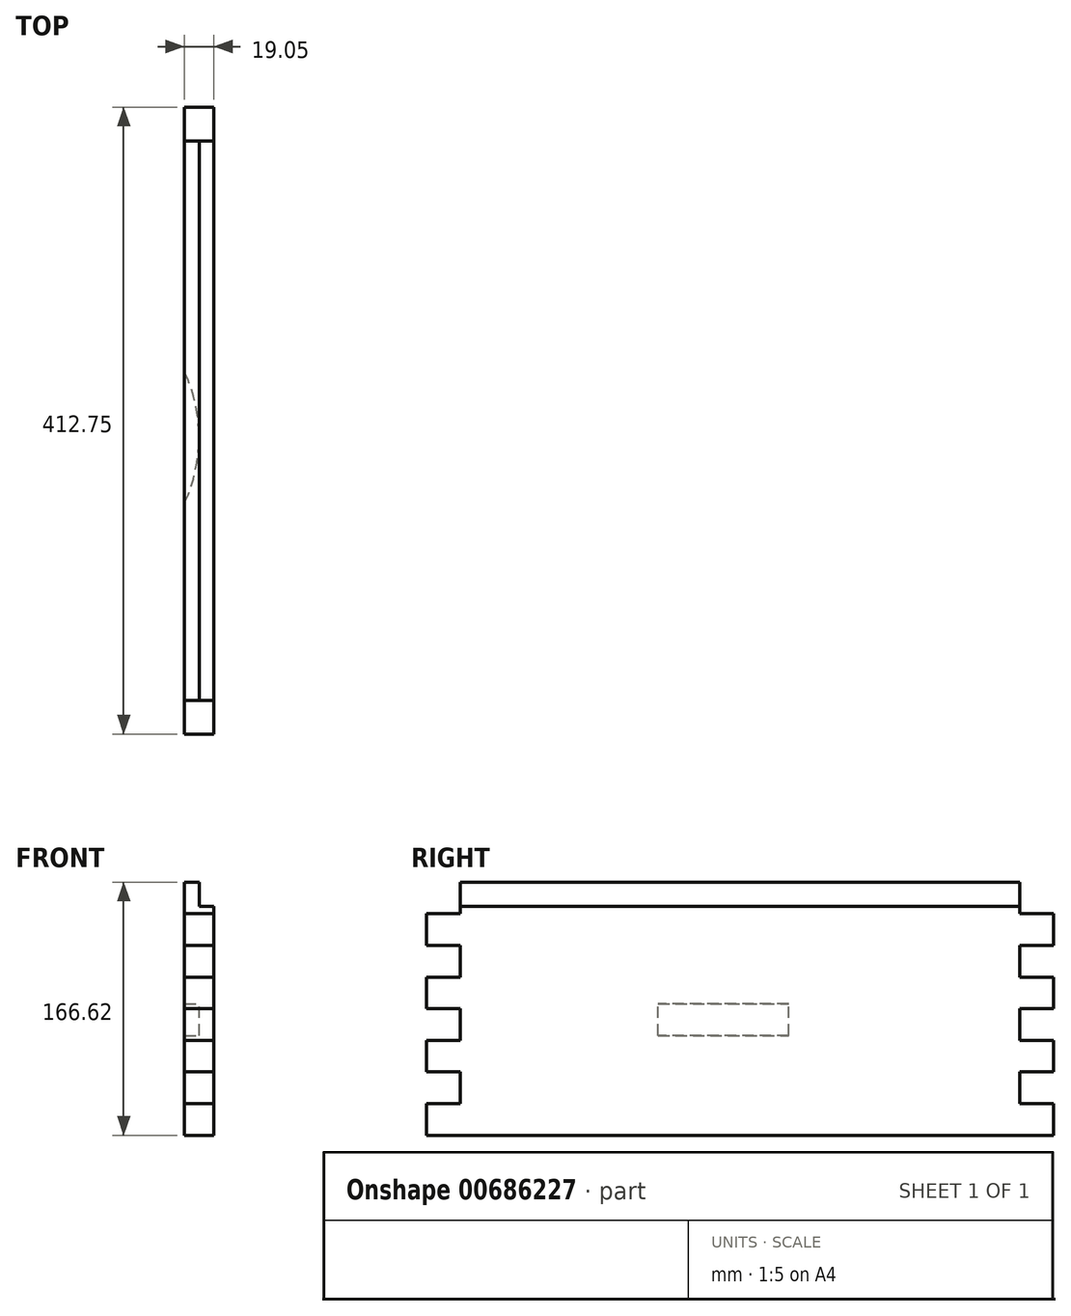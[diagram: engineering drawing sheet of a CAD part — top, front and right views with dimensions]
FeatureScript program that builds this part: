
annotation { "Feature Type Name" : "Feature", "Feature Type Description" : "" }
export const myFeature = defineFeature(function(context is Context, id is Id, definition is map)
    precondition{}
    {
        {
            var Q0;
            Q0=qCreatedBy(makeId("Front.planeOp"),FACE);
            var sketch = newSketch(context, id + "F0", { "sketchPlane" : qUnion([Q0])});
            skLineSegment(sketch, "E0.bottom", {"start": v(0, 0) * mm, "end": v(-19.05, 0) * mm});
            skLineSegment(sketch, "E0.top", {"start": v(0, 166.62) * mm, "end": v(-19.05, 166.62) * mm});
            skLineSegment(sketch, "E0.left", {"start": v(0, 0) * mm, "end": v(0, 166.62) * mm});
            skLineSegment(sketch, "E0.right", {"start": v(-19.05, 0) * mm, "end": v(-19.05, 166.62) * mm});
            skSolve(sketch);
        }
        {
            var Q0;
            Q0 = qSketchRegion(id + "F0", true);
            extrude(context, id + "F1", {"entities" : qUnion([Q0]), "oppositeDirection" : true, "depth" : 206.38 * mm, "offsetDistance" : 25.4 * mm});
        }
        {
            var Q0;
            Q0=qCreatedBy(makeId("Right.planeOp"),FACE);
            var sketch = newSketch(context, id + "F2", { "sketchPlane" : qUnion([Q0])});
            skLineSegment(sketch, "E1.bottom", {"start": v(0, 20.83) * mm, "end": v(22.23, 20.83) * mm});
            skLineSegment(sketch, "E1.top", {"start": v(0, 41.66) * mm, "end": v(22.23, 41.66) * mm});
            skLineSegment(sketch, "E1.left", {"start": v(0, 20.83) * mm, "end": v(0, 41.66) * mm});
            skLineSegment(sketch, "E1.right", {"start": v(22.23, 20.83) * mm, "end": v(22.23, 41.66) * mm});
            skLineSegment(sketch, "E2.bottom", {"start": v(0, 62.48) * mm, "end": v(22.23, 62.48) * mm});
            skLineSegment(sketch, "E2.top", {"start": v(0, 83.31) * mm, "end": v(22.23, 83.31) * mm});
            skLineSegment(sketch, "E2.left", {"start": v(0, 62.48) * mm, "end": v(0, 83.31) * mm});
            skLineSegment(sketch, "E2.right", {"start": v(22.23, 62.48) * mm, "end": v(22.23, 83.31) * mm});
            skLineSegment(sketch, "E3.bottom", {"start": v(0, 104.14) * mm, "end": v(22.23, 104.14) * mm});
            skLineSegment(sketch, "E3.top", {"start": v(0, 124.97) * mm, "end": v(22.23, 124.97) * mm});
            skLineSegment(sketch, "E3.left", {"start": v(0, 104.14) * mm, "end": v(0, 124.97) * mm});
            skLineSegment(sketch, "E3.right", {"start": v(22.23, 104.14) * mm, "end": v(22.22, 124.97) * mm});
            skLineSegment(sketch, "E4.bottom", {"start": v(0, 145.8) * mm, "end": v(22.22, 145.8) * mm});
            skLineSegment(sketch, "E4.top", {"start": v(0, 166.62) * mm, "end": v(22.22, 166.62) * mm});
            skLineSegment(sketch, "E4.left", {"start": v(0, 145.8) * mm, "end": v(0, 166.62) * mm});
            skLineSegment(sketch, "E4.right", {"start": v(22.22, 145.8) * mm, "end": v(22.22, 166.62) * mm});
            skLineSegment(sketch, "E5", {"start": v(22.22, 145.8) * mm, "end": v(22.23, 124.97) * mm, "construction": true});
            skLineSegment(sketch, "E6", {"start": v(22.23, 104.14) * mm, "end": v(22.23, 83.31) * mm, "construction": true});
            skLineSegment(sketch, "E7", {"start": v(22.23, 62.48) * mm, "end": v(22.23, 41.66) * mm, "construction": true});
            skLineSegment(sketch, "E8", {"start": v(22.23, 20.83) * mm, "end": v(22.23, 0) * mm, "construction": true});
            skSolve(sketch);
        }
        {
            var Q0;
            Q0 = qSketchRegion(id + "F2", true);
            extrude(context, id + "F3", {"entities" : qUnion([Q0]), "operationType" : NewBodyOperationType.REMOVE, "endBound" : BoundingType.THROUGH_ALL, "oppositeDirection" : true, "depth" : 25.4 * mm, "offsetDistance" : 25.4 * mm});
        }
        {
            var Q0;
            Q0=makeQuery(id+"F1.opExtrude","SWEPT_BODY",BODY,{"disambiguationData":[OSD([sQuery(id+"F0.wireOp",EDGE,"E0.bottom"),sQuery(id+"F0.wireOp",EDGE,"E0.top"),sQuery(id+"F0.wireOp",EDGE,"E0.left"),sQuery(id+"F0.wireOp",EDGE,"E0.right")])]});
            var Q1;
            Q1=makeQuery(id+"F1.opExtrude","CAP_FACE",FACE,{"disambiguationData":[OSD([sQuery(id+"F0.wireOp",EDGE,"E0.bottom"),sQuery(id+"F0.wireOp",EDGE,"E0.top"),sQuery(id+"F0.wireOp",EDGE,"E0.left"),sQuery(id+"F0.wireOp",EDGE,"E0.right")])],"isStart":false});
            mirror(context, id + "F4", {"operationType" : NewBodyOperationType.ADD, "entities" : qUnion([Q0]), "mirrorPlane" : qUnion([Q1])});
        }
        {
            var Q0;
            Q0=qCreatedBy(makeId("Front.planeOp"),FACE);
            var sketch = newSketch(context, id + "F5", { "sketchPlane" : qUnion([Q0])});
            skLineSegment(sketch, "E9.bottom", {"start": v(-9.53, 166.62) * mm, "end": v(0, 166.62) * mm});
            skLineSegment(sketch, "E9.top", {"start": v(-9.53, 150.75) * mm, "end": v(0, 150.75) * mm});
            skLineSegment(sketch, "E9.left", {"start": v(-9.53, 166.62) * mm, "end": v(-9.53, 150.75) * mm});
            skLineSegment(sketch, "E9.right", {"start": v(0, 166.62) * mm, "end": v(0, 150.75) * mm});
            skSolve(sketch);
        }
        {
            var Q0;
            Q0 = qSketchRegion(id + "F5", true);
            extrude(context, id + "F6", {"entities" : qUnion([Q0]), "operationType" : NewBodyOperationType.REMOVE, "endBound" : BoundingType.THROUGH_ALL, "oppositeDirection" : true, "depth" : 25.4 * mm, "offsetDistance" : 25.4 * mm});
        }
        {
            var Q0;
            Q0=qCreatedBy(makeId("Top.planeOp"),FACE);
            cPlane(context, id + "F7", {"entities" : qUnion([Q0]), "cplaneType" : CPlaneType.OFFSET, "offset" : 76.2 * mm, "width" : 152.4 * mm, "height" : 152.4 * mm});
        }
        {
            var Q0;
            Q0=qCreatedBy(id+"F7.planeOp",FACE);
            var sketch = newSketch(context, id + "F8", { "sketchPlane" : qUnion([Q0])});
            skCircle(sketch, "E10", {"center": v(-111.13, 195.26) * mm, "radius": 101.6 * mm});
            skLineSegment(sketch, "E11", {"start": v(-19.05, 390.53) * mm, "end": v(-19.05, 0) * mm, "construction": true});
            skLineSegment(sketch, "E12", {"start": v(-111.13, 195.26) * mm, "end": v(-19.05, 195.26) * mm, "construction": true});
            skSolve(sketch);
        }
        {
            var Q0;
            Q0 = qSketchRegion(id + "F8", true);
            extrude(context, id + "F9", {"entities" : qUnion([Q0]), "operationType" : NewBodyOperationType.REMOVE, "endBound" : BoundingType.SYMMETRIC, "oppositeDirection" : true, "depth" : 20.98 * mm, "offsetDistance" : 25.4 * mm});
        }
    });
